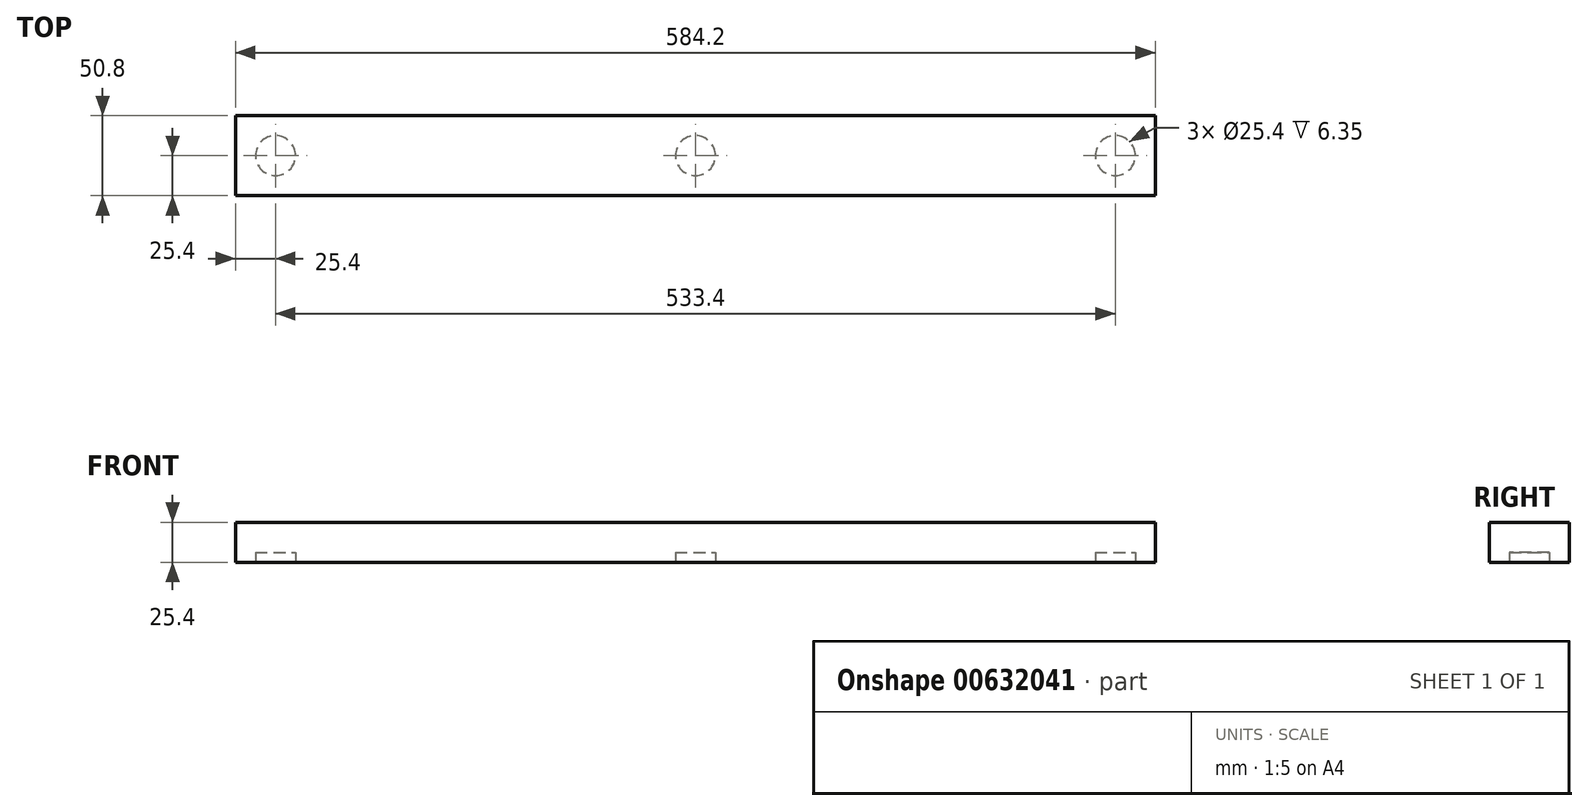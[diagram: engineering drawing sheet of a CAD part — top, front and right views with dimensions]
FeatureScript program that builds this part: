
annotation { "Feature Type Name" : "Feature", "Feature Type Description" : "" }
export const myFeature = defineFeature(function(context is Context, id is Id, definition is map)
    precondition{}
    {
        {
            var Q0;
            Q0=qCreatedBy(makeId("Front.planeOp"),FACE);
            var sketch = newSketch(context, id + "F0", { "sketchPlane" : qUnion([Q0])});
            skLineSegment(sketch, "E0.bottom", {"start": v(0, 0) * mm, "end": v(584.2, 0) * mm});
            skLineSegment(sketch, "E0.top", {"start": v(0, 25.4) * mm, "end": v(584.2, 25.4) * mm});
            skLineSegment(sketch, "E0.left", {"start": v(0, 0) * mm, "end": v(0, 25.4) * mm});
            skLineSegment(sketch, "E0.right", {"start": v(584.2, 0) * mm, "end": v(584.2, 25.4) * mm});
            skSolve(sketch);
        }
        {
            var Q0;
            Q0 = qSketchRegion(id + "F0", true);
            extrude(context, id + "F1", {"entities" : qUnion([Q0]), "depth" : 50.8 * mm, "offsetDistance" : 25.4 * mm});
        }
        {
            var Q0;
            Q0=makeQuery(id+"F1.opExtrude","SWEPT_FACE",FACE,{"disambiguationData":[OSD([sQuery(id+"F0.wireOp",EDGE,"E0.bottom")])]});
            var sketch = newSketch(context, id + "F2", { "sketchPlane" : qUnion([Q0])});
            skCircle(sketch, "E1", {"center": v(25.4, 25.4) * mm, "radius": 12.7 * mm});
            skPoint(sketch, "E1.centerSnap0", {"position": v(0, 25.4) * mm});
            skCircle(sketch, "E2", {"center": v(292.1, 25.4) * mm, "radius": 12.7 * mm});
            skPoint(sketch, "E2.centerSnap0", {"position": v(292.1, 0) * mm});
            skCircle(sketch, "E3", {"center": v(558.8, 25.4) * mm, "radius": 12.7 * mm});
            skPoint(sketch, "E3.centerSnap0", {"position": v(584.2, 25.4) * mm});
            skSolve(sketch);
        }
        {
            var Q0;
            Q0 = qSketchRegion(id + "F2", true);
            extrude(context, id + "F3", {"entities" : qUnion([Q0]), "operationType" : NewBodyOperationType.REMOVE, "oppositeDirection" : true, "depth" : 6.35 * mm, "offsetDistance" : 25.4 * mm});
        }
    });
